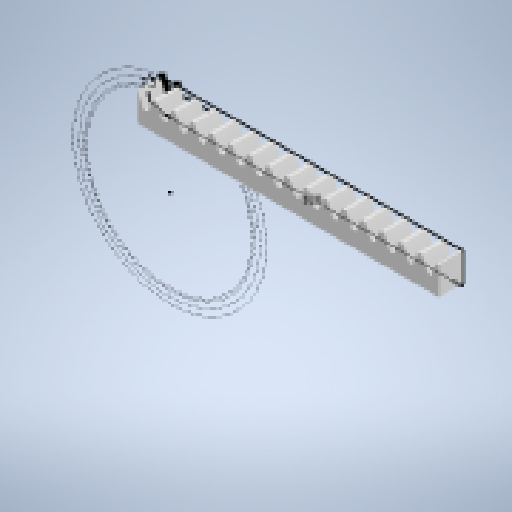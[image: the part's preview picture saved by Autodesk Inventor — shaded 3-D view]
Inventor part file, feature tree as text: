
AUTODESK INVENTOR PART (.ipt)
format: ipt  version: 2023 (Build 270158000, 158)  size: 335,360 bytes
history: native  units: mm
features: extrude x2, pattern_linear x1
ambient origin geometry x8: Origin, YZ Plane, XZ Plane, XY Plane, X Axis, Y Axis, Z Axis, Center Point
bodies: Body1 (feature_tree)
feature tree (3):
  extrude  "Extrusion2"  Depth=100.0mm
  extrude  "Extrusion3"  Depth=8.0mm TaperAngle=0.0deg
  pattern_linear  "Rectangular Pattern1"  Spacing1=0.0mm  [1 undecoded]
note: 1 required parameter value undecoded (feature->parameter linkage not recoverable at this tier; creation-order binding heuristic only, values carry confidence <= 0.55)
